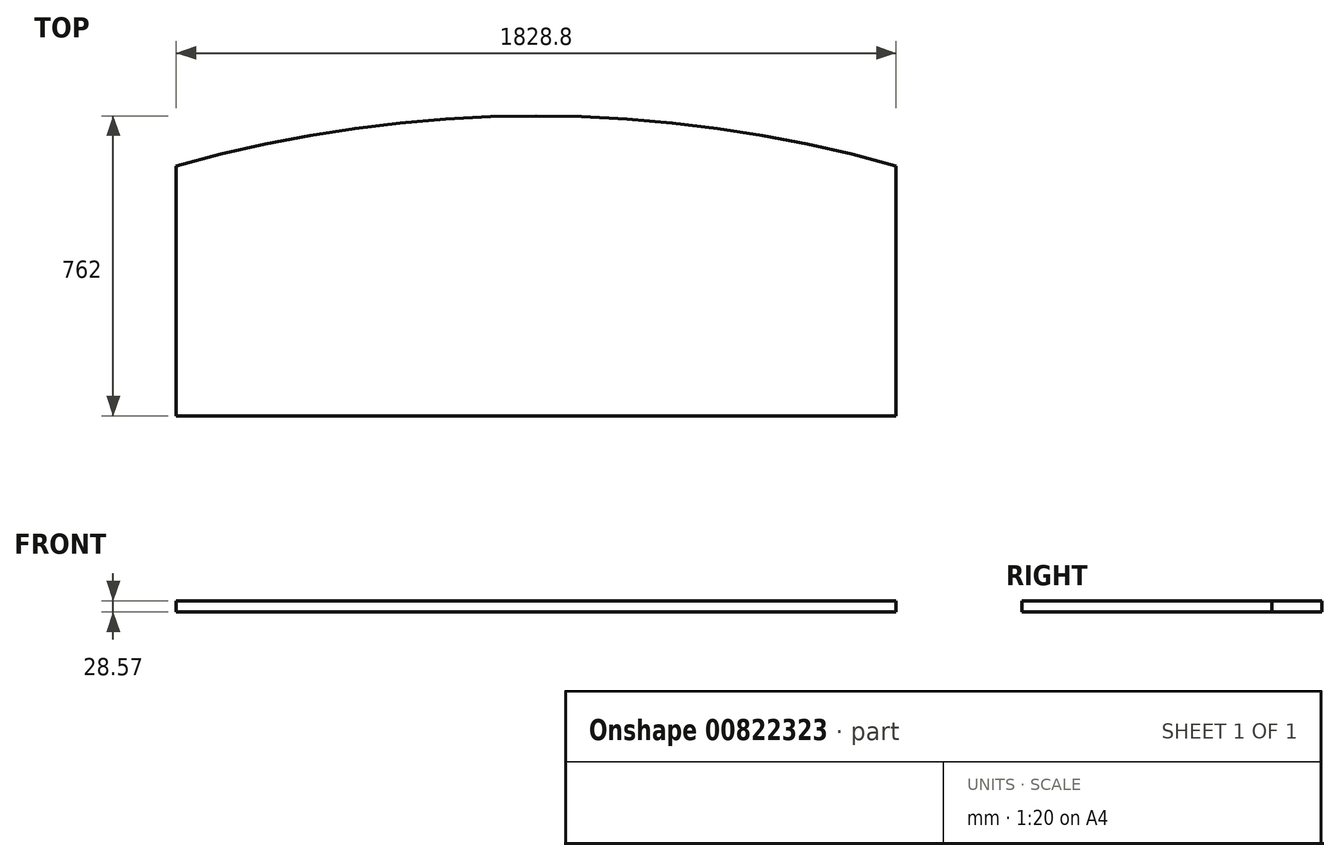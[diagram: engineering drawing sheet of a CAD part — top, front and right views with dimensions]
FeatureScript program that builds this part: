
annotation { "Feature Type Name" : "Feature", "Feature Type Description" : "" }
export const myFeature = defineFeature(function(context is Context, id is Id, definition is map)
    precondition{}
    {
        {
            var Q0;
            Q0=qCreatedBy(makeId("Top.planeOp"),FACE);
            var sketch = newSketch(context, id + "F0", { "sketchPlane" : qUnion([Q0])});
            skLineSegment(sketch, "E0.bottom", {"start": v(-914.4, 317.5) * mm, "end": v(914.4, 317.5) * mm});
            skLineSegment(sketch, "E0.top", {"start": v(-914.4, -317.5) * mm, "end": v(914.4, -317.5) * mm});
            skLineSegment(sketch, "E0.left", {"start": v(-914.4, 317.5) * mm, "end": v(-914.4, -317.5) * mm});
            skLineSegment(sketch, "E0.right", {"start": v(914.4, 317.5) * mm, "end": v(914.4, -317.5) * mm});
            skPoint(sketch, "E0.middle", {"position": v(0, 0) * mm});
            skLineSegment(sketch, "E1", {"start": v(0, 317.5) * mm, "end": v(0, 444.5) * mm});
            skArc(sketch, "E2", {"start": v(914.4, 317.5) * mm, "mid": v(0, 444.5) * mm, "end": v(-914.4, 317.5) * mm});
            skSolve(sketch);
        }
        {
            var Q0;
            Q0=makeQuery(id+"F0.imprint","IMPRINT",FACE,{"disambiguationData":[TD([[makeQuery(id+"F0.imprint","IMPRINT",EDGE,{"derivedFrom":sQuery(id+"F0.wireOp",EDGE,"E0.bottom")}),-1.0]])]});
            var Q1;
            {var subQ3=sQuery(id+"F0.wireOp",EDGE,"E1");Q1=makeQuery(id+"F0.imprint","IMPRINT",FACE,{"disambiguationData":[TD([[makeQuery(id+"F0.imprint","IMPRINT",EDGE,{"derivedFrom":subQ3}),1.0]])]});}
            var Q2;
            {var subQ3=sQuery(id+"F0.wireOp",EDGE,"E1");Q2=makeQuery(id+"F0.imprint","IMPRINT",FACE,{"disambiguationData":[TD([[makeQuery(id+"F0.imprint","IMPRINT",EDGE,{"derivedFrom":subQ3}),-1.0]])]});}
            extrude(context, id + "F1", {"entities" : qUnion([Q0, Q1, Q2]), "depth" : 28.57 * mm, "offsetDistance" : 25.4 * mm});
        }
    });
